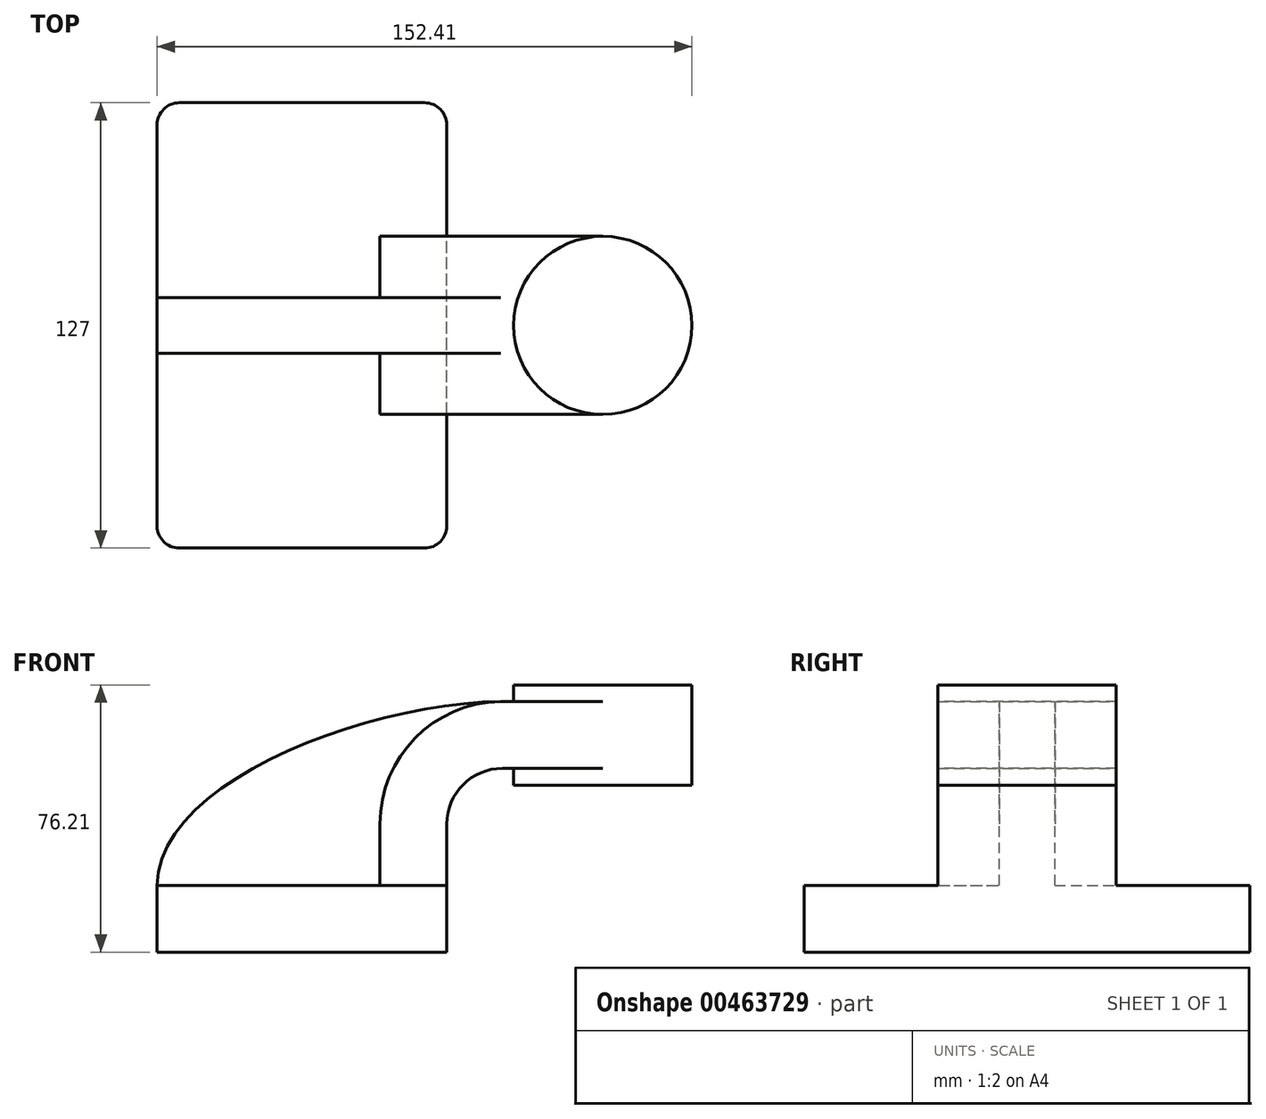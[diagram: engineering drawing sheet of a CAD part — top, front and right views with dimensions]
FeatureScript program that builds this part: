
annotation { "Feature Type Name" : "Feature", "Feature Type Description" : "" }
export const myFeature = defineFeature(function(context is Context, id is Id, definition is map)
    precondition{}
    {
        {
            var Q0;
            Q0=qCreatedBy(makeId("Front.planeOp"),FACE);
            var sketch = newSketch(context, id + "F0", { "sketchPlane" : qUnion([Q0])});
            skLineSegment(sketch, "E0.bottom", {"start": v(41.27, 9.53) * mm, "end": v(-41.28, 9.53) * mm});
            skLineSegment(sketch, "E0.top", {"start": v(41.28, -9.52) * mm, "end": v(-41.27, -9.52) * mm});
            skLineSegment(sketch, "E0.left", {"start": v(41.28, 9.53) * mm, "end": v(41.28, -9.52) * mm});
            skLineSegment(sketch, "E0.right", {"start": v(-41.28, 9.53) * mm, "end": v(-41.27, -9.52) * mm});
            skPoint(sketch, "E0.middle", {"position": v(0, 0) * mm});
            skLineSegment(sketch, "E1.bottom", {"start": v(111.12, 38.1) * mm, "end": v(60.33, 38.1) * mm});
            skLineSegment(sketch, "E1.top", {"start": v(111.13, 66.68) * mm, "end": v(60.33, 66.68) * mm});
            skLineSegment(sketch, "E1.left", {"start": v(111.12, 38.1) * mm, "end": v(111.12, 66.68) * mm});
            skLineSegment(sketch, "E1.right", {"start": v(60.33, 38.1) * mm, "end": v(60.33, 66.68) * mm});
            skPoint(sketch, "E1.middle", {"position": v(85.73, 52.39) * mm});
            skLineSegment(sketch, "E2", {"start": v(41.27, 9.53) * mm, "end": v(41.27, 27) * mm});
            skArc(sketch, "E3", {"start": v(41.27, 27) * mm, "mid": v(45.92, 38.23) * mm, "end": v(57.15, 42.88) * mm});
            skLineSegment(sketch, "E4", {"start": v(57.15, 42.88) * mm, "end": v(85.72, 42.88) * mm});
            skLineSegment(sketch, "E5.0", {"start": v(57.15, 61.93) * mm, "end": v(85.72, 61.93) * mm});
            skArc(sketch, "E5.1", {"start": v(22.23, 27) * mm, "mid": v(32.45, 51.7) * mm, "end": v(57.15, 61.93) * mm});
            skLineSegment(sketch, "E5.2", {"start": v(22.22, 9.53) * mm, "end": v(22.22, 27) * mm});
            skLineSegment(sketch, "E6", {"start": v(85.73, 66.68) * mm, "end": v(85.73, 38.1) * mm});
            skFitSpline(sketch, "E7", {"points": [v(-41.28, 9.52) * mm, v(57.15, 61.93) * mm], "startDerivative": vector(0.75, 88.72) * mm, "endDerivative": vector(115.32, 0.6) * mm});
            skSolve(sketch);
        }
        {
            var Q0;
            Q0=makeQuery(id+"F0.imprint","IMPRINT",FACE,{"disambiguationData":[TD([[makeQuery(id+"F0.imprint","IMPRINT",EDGE,{"derivedFrom":sQuery(id+"F0.wireOp",EDGE,"E0.top")}),-1.0]])]});
            extrude(context, id + "F1", {"entities" : qUnion([Q0]), "depth" : 127 * mm, "symmetric" : true});
        }
        {
            var Q0;
            {var subQ1=sQuery(id+"F0.wireOp",EDGE,"E2");Q0=makeQuery(id+"F0.imprint","IMPRINT",FACE,{"disambiguationData":[TD([[makeQuery(id+"F0.imprint","IMPRINT",EDGE,{"derivedFrom":subQ1}),1.0]])]});}
            var Q1;
            {var subQ0=sQuery(id+"F0.wireOp",EDGE,"E4");var subQ1=sQuery(id+"F0.wireOp",EDGE,"E1.right");var subQ2=makeQuery(id+"F0.imprint","INTERSECT",VERTEX,{"derivedFrom":[subQ1,subQ0]});Q1=makeQuery(id+"F0.imprint","IMPRINT",FACE,{"disambiguationData":[TD([[makeQuery(id+"F0.imprint","IMPRINT",EDGE,{"disambiguationData":[TD([[subQ2,-1.0]])],"derivedFrom":subQ1}),-1.0]])]});}
            extrude(context, id + "F2", {"entities" : qUnion([Q0, Q1]), "operationType" : NewBodyOperationType.ADD, "depth" : 50.8 * mm, "symmetric" : true});
        }
        {
            var Q0;
            {var subQ3=sQuery(id+"F0.wireOp",EDGE,"E5.2");Q0=makeQuery(id+"F0.imprint","IMPRINT",FACE,{"disambiguationData":[TD([[makeQuery(id+"F0.imprint","IMPRINT",EDGE,{"derivedFrom":subQ3}),1.0]])]});}
            extrude(context, id + "F3", {"entities" : qUnion([Q0]), "operationType" : NewBodyOperationType.ADD, "depth" : 15.88 * mm, "symmetric" : true});
        }
        {
            var Q0;
            {var subQ0=sQuery(id+"F0.wireOp",EDGE,"E1.left");Q0=makeQuery(id+"F0.imprint","IMPRINT",FACE,{"disambiguationData":[TD([[makeQuery(id+"F0.imprint","IMPRINT",EDGE,{"derivedFrom":subQ0}),1.0]])]});}
            var Q1;
            Q1=sQuery(id+"F0.wireOp",EDGE,"E6");
            revolve(context, id + "F4", {"operationType" : NewBodyOperationType.ADD, "entities" : qUnion([Q0]), "axis" : qUnion([Q1]), "revolveType" : RevolveType.FULL});
        }
        {
            var Q0;
            Q0=makeQuery(id+"F1.opExtrude","CAP_EDGE",EDGE,{"disambiguationData":[OSD([sQuery(id+"F0.wireOp",EDGE,"E0.left")])],"isStart":false});
            var Q1;
            Q1=makeQuery(id+"F1.opExtrude","CAP_EDGE",EDGE,{"disambiguationData":[OSD([sQuery(id+"F0.wireOp",EDGE,"E0.right")])],"isStart":false});
            var Q2;
            Q2=makeQuery(id+"F1.opExtrude","CAP_EDGE",EDGE,{"disambiguationData":[OSD([sQuery(id+"F0.wireOp",EDGE,"E0.right")])],"isStart":true});
            var Q3;
            Q3=makeQuery(id+"F1.opExtrude","CAP_EDGE",EDGE,{"disambiguationData":[OSD([sQuery(id+"F0.wireOp",EDGE,"E0.left")])],"isStart":true});
            fillet(context, id + "F5", {"entities" : qUnion([Q0, Q1, Q2, Q3]), "radius" : 6.35 * mm, "tangentPropagation" : true, "allowEdgeOverflow" : false});
        }
    });
